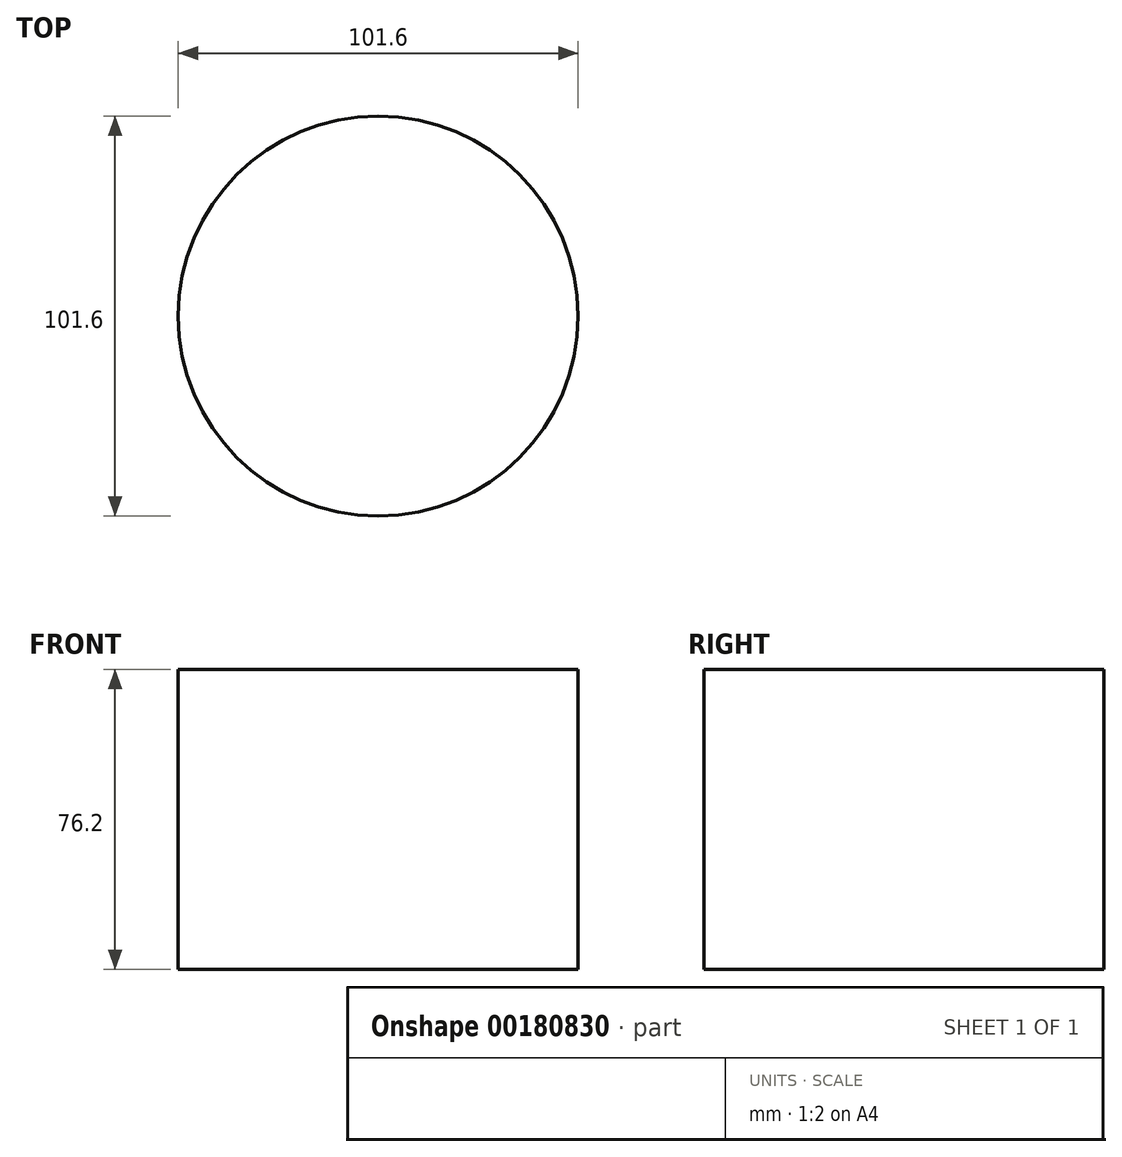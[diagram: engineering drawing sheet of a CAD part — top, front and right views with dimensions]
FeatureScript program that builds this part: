
annotation { "Feature Type Name" : "Feature", "Feature Type Description" : "" }
export const myFeature = defineFeature(function(context is Context, id is Id, definition is map)
    precondition{}
    {
        {
            var Q0;
            Q0=qCreatedBy(makeId("Top.planeOp"),FACE);
            cPlane(context, id + "F0", {"entities" : qUnion([Q0]), "cplaneType" : CPlaneType.OFFSET, "offset" : 76.2 * mm, "oppositeDirection" : true, "width" : 152.4 * mm, "height" : 152.4 * mm});
        }
        {
            var Q0;
            Q0=qCreatedBy(makeId("Top.planeOp"),FACE);
            var sketch = newSketch(context, id + "F1", { "sketchPlane" : qUnion([Q0])});
            skCircle(sketch, "E0", {"center": v(0, -0.66) * mm, "radius": 50.8 * mm});
            skSolve(sketch);
        }
        {
            var Q0;
            Q0=makeQuery(id+"F1.imprint","IMPRINT",FACE,{"disambiguationData":[TD([[makeQuery(id+"F1.imprint","IMPRINT",EDGE,{"derivedFrom":sQuery(id+"F1.wireOp",EDGE,"E0")}),1.0]])]});
            extrude(context, id + "F2", {"entities" : qUnion([Q0]), "oppositeDirection" : true, "depth" : 76.2 * mm});
        }
    });
